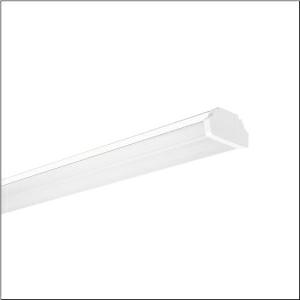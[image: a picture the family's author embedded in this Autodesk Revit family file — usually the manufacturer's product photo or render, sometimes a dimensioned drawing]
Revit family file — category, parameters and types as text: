
# Revit family: dus_r__31_ho_53bd812m1v4120_db1b
name_source: partatom
category: Lighting Fixtures
units: mm (PartAtom-declared; Revit-internal decimal feet)

## family parameters
Cut with Voids When Loaded = No
Host = Face
Light Source = No
Part Type = Normal
Room Calculation Point = No
Round Connector Dimension = Use Diameter
Shared = No

## types (1)
- --- (1 x LED, 12380 lm, 77.3 W, 4000K)
    Apparent Load = 77 VA
    CIE Flux Codes = 47 80 95 92 100
    Color Rendering = 80
    Color Temperature = 4000K
    Default Elevation = 1800 mm
    Description = DUS® 31 HO, luminaire insert, of sheet steel, coil coated, white, length: 1.535mm, width: 81mm, height: 90mm, 5x system unit, system units: 307mm, LED rated luminous flux: 12.380lm, light colour: 840, control gear: ON/OFF Multilumen, control gear: ECG Multilumen, with plug, 3-pole, with phase selection, mains connection: 220..240V, AC, 50/60Hz, rated input power: 77W, through-wiring accessed according to module size, primary optical cover: cover, of PMMA, light emission: direct distribution, primary light characteristic: symmetric, protection rating (complete): IP20, protection rating (LED compartment): IP50, insulation class (complete): insulation class I (protective earthing), certification: CE, ENEC, VDE, UKCA, impact resistance: IK03, permissible ambient temperature for indoor applications: -35..+35°C, corresponds to IFS (International Featured Standards) requirements for safety and quality in the food industry, reducing of maximum allowable ambient temperature of 5°C with ceiling mounting, packaging unit: 1 piece
    Height = 95 mm
    Lamp = 1 x LED
    Lamp Light Flux = 12380 lm
    Lamp Power = 77.3 W
    Lamp count = 1
    Length = 1535 mm
    Luminous efficacy = 160 lm/W
    Manufacturer = Siteco
    ModVariant = No
    Model = 53BD812M1V4120
    Mounting Place = Ceiling
    Mounting Type = Pendant
    Number of Poles = 1
    OnlyDefault = Yes
    Power Factor = 1
    Product Name = DUS® 31 HO
    Product group = luminaire insert
    ProductGroupID = 901
    Protection Class = Protection class I
    Protection Degree = IP 20
    RLX_Detail_Level = 1
    RLX_Emergency_Light_Flux = 0 lm
    RLX_Emergency_Type = 0
    RLX_Emergency_Type_DB = No
    RlxData = <blob elided: 39821 chars, md5=cbcaf8a0>
    Socket = socket
    Standby Power = 0 W
    System Light Flux = 12380 lm
    System Power = 77 W
    Type Comments = factory setting: luminous flux: 100 % | (A | C | E) | 173 mA
    Type Image = l_1313537.jpg
    URL = http://relux.com
    VarID = @adj_156115
    Voltage = 0 V
    Weight = 0.00 kg
    Width = 81 mm

## geometry (parser evidence)
native form markers: Blend x4, Sweep x11
no freeform markers — native parametric forms only
